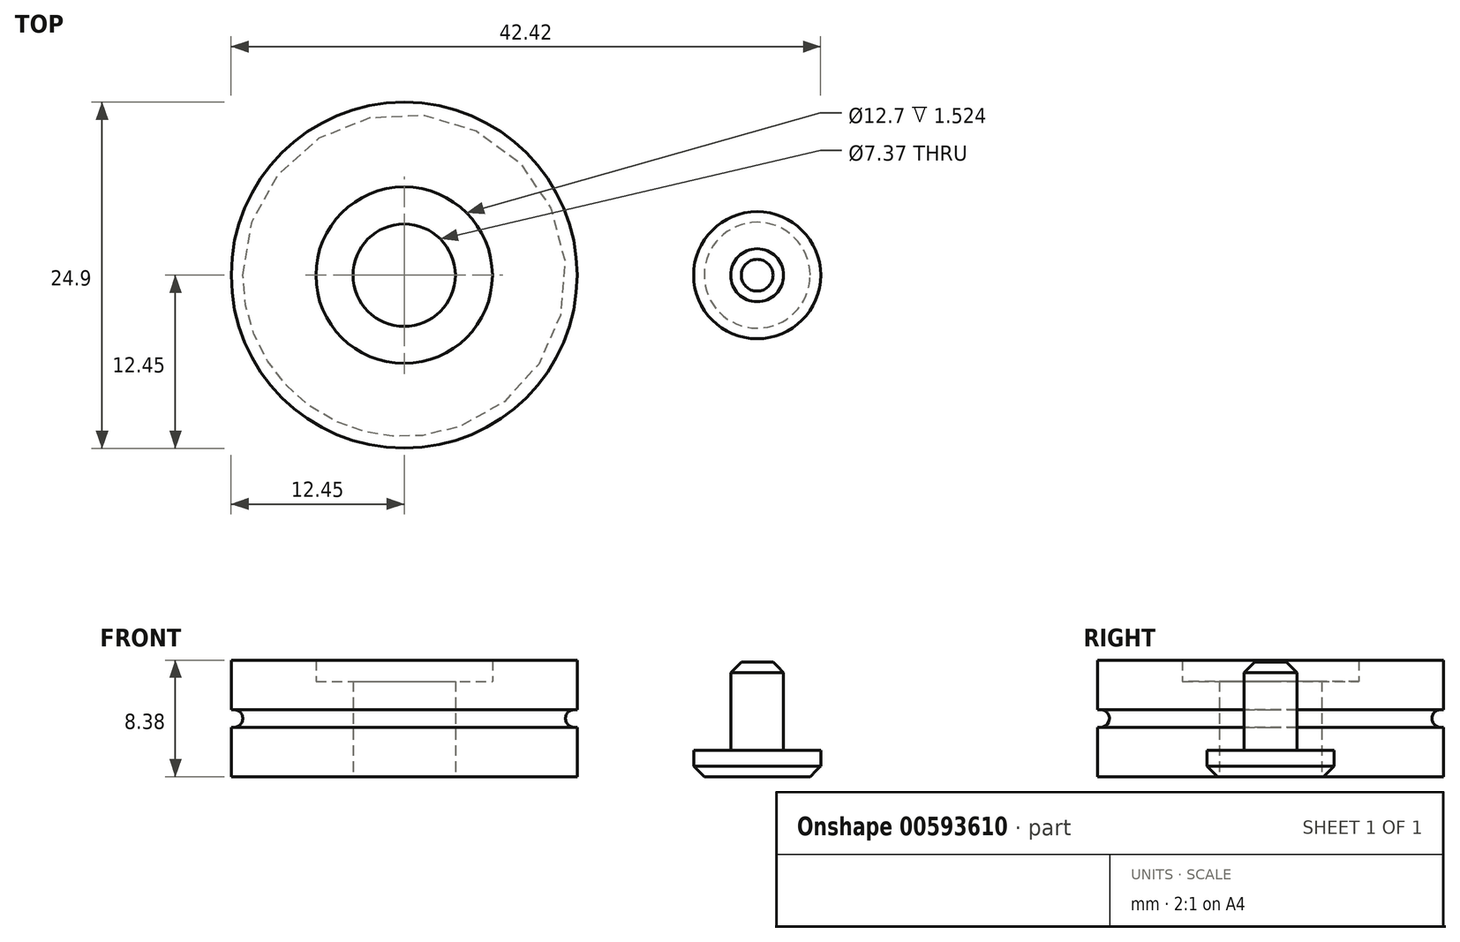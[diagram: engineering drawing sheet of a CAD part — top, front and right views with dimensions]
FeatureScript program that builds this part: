
annotation { "Feature Type Name" : "Feature", "Feature Type Description" : "" }
export const myFeature = defineFeature(function(context is Context, id is Id, definition is map)
    precondition{}
    {
        {
            var Q0;
            Q0=qCreatedBy(makeId("Front.planeOp"),FACE);
            var sketch = newSketch(context, id + "F0", { "sketchPlane" : qUnion([Q0])});
            skLineSegment(sketch, "E0", {"start": v(0, 0) * mm, "end": v(0, 16.56) * mm, "construction": true});
            skLineSegment(sketch, "E1", {"start": v(-3.68, 0) * mm, "end": v(-12.45, 0) * mm});
            skLineSegment(sketch, "E2", {"start": v(-12.45, 0) * mm, "end": v(-12.45, 3.56) * mm});
            skLineSegment(sketch, "E3", {"start": v(-12.45, 8.38) * mm, "end": v(-6.35, 8.38) * mm});
            skArc(sketch, "E4", {"start": v(-12.24, 3.56) * mm, "mid": v(-11.6, 4.2) * mm, "end": v(-12.24, 4.83) * mm});
            skLineSegment(sketch, "E5.trimOffspring", {"start": v(-12.45, 4.83) * mm, "end": v(-12.45, 8.38) * mm});
            skLineSegment(sketch, "E6", {"start": v(-3.68, 6.86) * mm, "end": v(-3.68, 0) * mm});
            skLineSegment(sketch, "E7.0", {"start": v(-6.35, 6.86) * mm, "end": v(-3.68, 6.86) * mm});
            skLineSegment(sketch, "E8.0", {"start": v(-6.35, 6.86) * mm, "end": v(-6.35, 8.38) * mm});
            skLineSegment(sketch, "E9", {"start": v(-12.24, 4.83) * mm, "end": v(-12.45, 4.83) * mm});
            skLineSegment(sketch, "E10", {"start": v(-12.45, 3.56) * mm, "end": v(-12.24, 3.56) * mm});
            skSolve(sketch);
        }
        {
            var Q0;
            Q0=qCreatedBy(makeId("Front.planeOp"),FACE);
            var sketch = newSketch(context, id + "F1", { "sketchPlane" : qUnion([Q0])});
            skLineSegment(sketch, "E11", {"start": v(20.83, 0) * mm, "end": v(25.4, 0) * mm});
            skLineSegment(sketch, "E12", {"start": v(25.4, 0) * mm, "end": v(25.4, 8.25) * mm});
            skLineSegment(sketch, "E13.0", {"start": v(20.83, 0) * mm, "end": v(20.83, 1.9) * mm});
            skLineSegment(sketch, "E14.0", {"start": v(20.83, 1.9) * mm, "end": v(23.5, 1.9) * mm});
            skLineSegment(sketch, "E15.0", {"start": v(23.5, 1.9) * mm, "end": v(23.5, 8.25) * mm});
            skLineSegment(sketch, "E16.trimOffspring", {"start": v(23.5, 8.26) * mm, "end": v(25.4, 8.26) * mm});
            skSolve(sketch);
        }
        {
            var Q0;
            Q0 = qSketchRegion(id + "F0", true);
            var Q1;
            Q1=sQuery(id+"F0.wireOp",EDGE,"E0");
            revolve(context, id + "F2", {"surfaceOperationType" : NewSurfaceOperationType.NEW, "entities" : qUnion([Q0]), "axis" : qUnion([Q1]), "revolveType" : RevolveType.FULL});
        }
        {
            var Q0;
            Q0=makeQuery(id+"F1.imprint","IMPRINT",FACE,{"disambiguationData":[TD([[makeQuery(id+"F1.imprint","IMPRINT",EDGE,{"derivedFrom":sQuery(id+"F1.wireOp",EDGE,"E11")}),1.0]])]});
            var Q1;
            Q1=sQuery(id+"F1.wireOp",EDGE,"E12");
            revolve(context, id + "F3", {"surfaceOperationType" : NewSurfaceOperationType.NEW, "entities" : qUnion([Q0]), "axis" : qUnion([Q1]), "revolveType" : RevolveType.FULL});
        }
        {
            var Q0;
            Q0=makeQuery(id+"F3.opRevolve","SWEPT_EDGE",EDGE,{"disambiguationData":[OSD([sQuery(id+"F1.wireOp",EDGE,"E15.0"),sQuery(id+"F1.wireOp",EDGE,"E16.trimOffspring")])]});
            var Q1;
            Q1=makeQuery(id+"F3.opRevolve","SWEPT_EDGE",EDGE,{"disambiguationData":[OSD([sQuery(id+"F1.wireOp",EDGE,"E11"),sQuery(id+"F1.wireOp",EDGE,"E13.0")])]});
            chamfer(context, id + "F4", {"entities" : qUnion([Q0, Q1]), "width" : 0.76 * mm, "tangentPropagation" : true});
        }
    });
